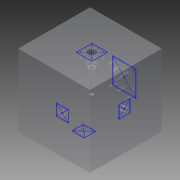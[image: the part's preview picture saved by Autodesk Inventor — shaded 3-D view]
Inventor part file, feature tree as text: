
AUTODESK INVENTOR PART (.ipt)
format: ipt  version: 2014 (Build 180170000, 170)  size: 503,296 bytes
history: native  units: mm
features: other x53, sketch x6, extrude x1
ambient origin geometry x8: Origin, YZ Plane, XZ Plane, XY Plane, X Axis, Y Axis, Z Axis, Center Point
bodies: 实体1 (feature_tree)
feature tree (60):
  extrude  "拉伸1"  TaperAngle=0.0deg  [1 undecoded]
  other  "UCS1"
  other  "UCS2"
  other  "UCS3"
  other  "UCS4"
  other  "UCS5"
  other  "UCS6"
  other  "Footprint2"
  other  "Footprint3"
  other  "Footprint4"
  other  "Footprint1"
  other  "Footprint5"
  sketch  "草图1"  dims[d0=300.0mm d1=0.0mm]
  other  "UCS1: YZ 平面"
  other  "UCS1: XZ 平面"
  other  "UCS1: XY 平面"
  other  "UCS1: X 轴"
  other  "UCS1: Y 轴"
  other  "UCS1: Z 轴"
  other  "UCS1: 原点"
  other  "UCS2: YZ 平面"
  other  "UCS2: XZ 平面"
  other  "UCS2: XY 平面"
  other  "UCS2: X 轴"
  other  "UCS2: Y 轴"
  other  "UCS2: Z 轴"
  other  "UCS2: 原点"
  other  "UCS3: YZ 平面"
  other  "UCS3: XZ 平面"
  other  "UCS3: XY 平面"
  other  "UCS3: X 轴"
  other  "UCS3: Y 轴"
  other  "UCS3: Z 轴"
  other  "UCS3: 原点"
  other  "UCS4: YZ 平面"
  other  "UCS4: XZ 平面"
  other  "UCS4: XY 平面"
  other  "UCS4: X 轴"
  other  "UCS4: Y 轴"
  other  "UCS4: Z 轴"
  other  "UCS4: 原点"
  other  "UCS5: YZ 平面"
  other  "UCS5: XZ 平面"
  other  "UCS5: XY 平面"
  other  "UCS5: X 轴"
  other  "UCS5: Y 轴"
  other  "UCS5: Z 轴"
  other  "UCS5: 原点"
  other  "UCS6: YZ 平面"
  other  "UCS6: XZ 平面"
  other  "UCS6: XY 平面"
  other  "UCS6: X 轴"
  other  "UCS6: Y 轴"
  other  "UCS6: Z 轴"
  other  "UCS6: 原点"
  sketch  "草图6"  dims[d8=0.0mm d9=0.0mm d10=0.0mm d11=0.0mm d12=0.0mm d13=0.0mm]
  sketch  "草图8"  dims[d14=0.0mm d15=0.0mm d16=0.0mm d17=0.0mm d18=0.0mm d19=0.0mm]
  sketch  "草图10"  dims[d20=0.0mm d21=0.0mm d22=0.0mm d23=0.0mm d24=0.0mm d25=0.0mm]
  sketch  "草图12"  dims[d26=0.0mm d27=0.0mm d28=0.0mm d29=0.0mm d30=0.0mm d31=0.0mm d32=0.0mm d33=0.0mm d34=0.0mm d35=0.0mm d36=0.0mm d37=0.0mm d38=0.0mm d44=0.0mm d58=0.0mm d72=0.0mm d73=0.0mm d92=0.0mm]
  sketch  "草图4"  dims[d2=0.0mm d3=0.0mm d4=0.0mm d5=0.0mm d6=0.0mm d7=0.0mm]
note: 1 required parameter value undecoded (feature->parameter linkage not recoverable at this tier; creation-order binding heuristic only, values carry confidence <= 0.55)
